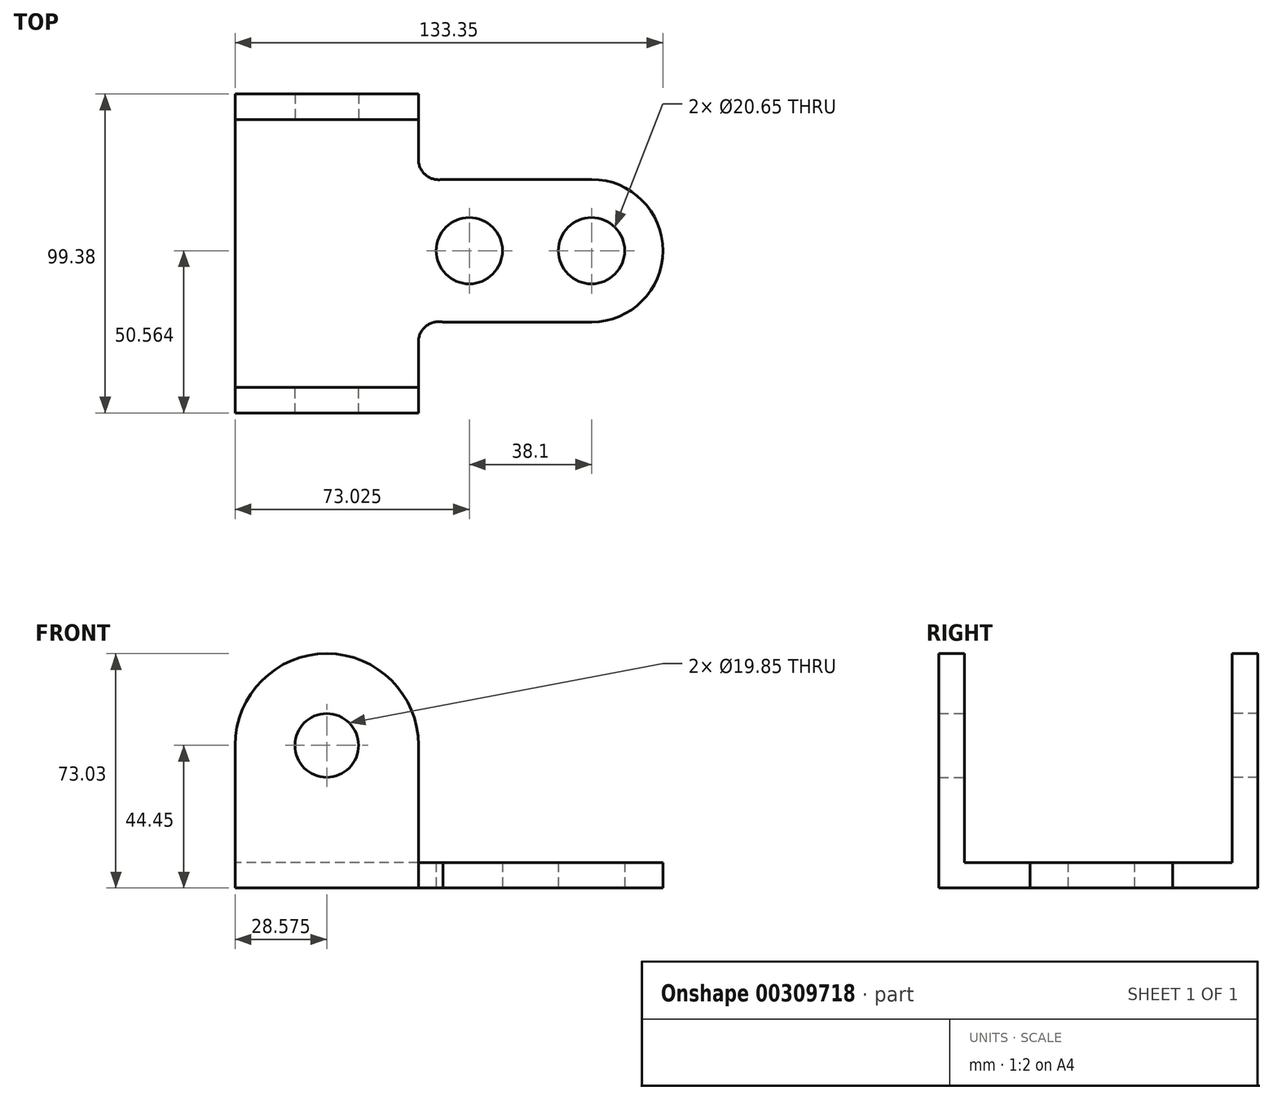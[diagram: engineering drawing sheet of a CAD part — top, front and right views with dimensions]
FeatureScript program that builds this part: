
annotation { "Feature Type Name" : "Feature", "Feature Type Description" : "" }
export const myFeature = defineFeature(function(context is Context, id is Id, definition is map)
    precondition{}
    {
        {
            var Q0;
            Q0=qCreatedBy(makeId("Top.planeOp"),FACE);
            var sketch = newSketch(context, id + "F0", { "sketchPlane" : qUnion([Q0])});
            skLineSegment(sketch, "E0", {"start": v(0, 0) * mm, "end": v(57.15, 0) * mm});
            skLineSegment(sketch, "E1", {"start": v(0, 18.14) * mm, "end": v(57.15, 18.14) * mm});
            skLineSegment(sketch, "E2", {"start": v(0, 0) * mm, "end": v(0, 91.44) * mm});
            skLineSegment(sketch, "E3", {"start": v(0, 91.44) * mm, "end": v(57.15, 91.44) * mm});
            skLineSegment(sketch, "E4", {"start": v(57.15, 91.44) * mm, "end": v(57.15, 75.04) * mm});
            skLineSegment(sketch, "E5", {"start": v(57.15, 75.04) * mm, "end": v(0, 75.04) * mm});
            skLineSegment(sketch, "E6", {"start": v(57.15, 18.14) * mm, "end": v(57.15, 0) * mm});
            skLineSegment(sketch, "E7", {"start": v(64.76, 68.82) * mm, "end": v(111.12, 68.82) * mm});
            skLineSegment(sketch, "E8", {"start": v(64.76, 24.37) * mm, "end": v(111.12, 24.37) * mm});
            skArc(sketch, "E9", {"start": v(111.12, 24.37) * mm, "mid": v(133.35, 46.6) * mm, "end": v(111.12, 68.82) * mm});
            skArc(sketch, "E10", {"start": v(57.15, 75.04) * mm, "mid": v(59.48, 70.13) * mm, "end": v(64.76, 68.82) * mm});
            skArc(sketch, "E11", {"start": v(64.76, 24.37) * mm, "mid": v(59.48, 23.06) * mm, "end": v(57.15, 18.14) * mm});
            skCircle(sketch, "E12", {"center": v(73.03, 46.6) * mm, "radius": 10.33 * mm});
            skCircle(sketch, "E13", {"center": v(111.12, 46.6) * mm, "radius": 10.33 * mm});
            skSolve(sketch);
        }
        {
            var Q0;
            Q0 = qSketchRegion(id + "F0", true);
            extrude(context, id + "F1", {"entities" : qUnion([Q0]), "depth" : 7.94 * mm});
        }
        {
            var Q0;
            Q0=makeQuery(id+"F1.opExtrude","SWEPT_FACE",FACE,{"disambiguationData":[OSD([sQuery(id+"F0.wireOp",EDGE,"E0")])]});
            var sketch = newSketch(context, id + "F2", { "sketchPlane" : qUnion([Q0])});
            skLineSegment(sketch, "E14", {"start": v(0, 0) * mm, "end": v(0, 44.45) * mm});
            skLineSegment(sketch, "E15", {"start": v(57.15, 0) * mm, "end": v(57.15, 44.45) * mm});
            skArc(sketch, "E16", {"start": v(57.15, 44.45) * mm, "mid": v(28.58, 73.03) * mm, "end": v(0, 44.45) * mm});
            skCircle(sketch, "E17", {"center": v(28.58, 44.45) * mm, "radius": 9.92 * mm});
            skSolve(sketch);
        }
        {
            var Q0;
            {var subQ1=sQuery(id+"F0.wireOp",EDGE,"E0");var subQ2=makeQuery(id+"F1.opExtrude","CAP_EDGE",EDGE,{"disambiguationData":[OSD([subQ1])],"isStart":true});Q0=makeQuery(id+"F2.imprint","IMPRINT",FACE,{"disambiguationData":[TD([[makeQuery(id+"F2.imprint","IMPRINT",EDGE,{"derivedFrom":subQ2}),1.0]])]});}
            var Q1;
            {var subQ0=sQuery(id+"F2.wireOp",EDGE,"E16");Q1=makeQuery(id+"F2.imprint","IMPRINT",FACE,{"disambiguationData":[TD([[makeQuery(id+"F2.imprint","IMPRINT",EDGE,{"derivedFrom":subQ0}),1.0]])]});}
            extrude(context, id + "F3", {"entities" : qUnion([Q0, Q1]), "operationType" : NewBodyOperationType.ADD, "endBound" : BoundingType.SYMMETRIC, "depth" : 7.94 * mm});
        }
        {
            var Q0;
            Q0=makeQuery(id+"F1.opExtrude","SWEPT_FACE",FACE,{"disambiguationData":[OSD([sQuery(id+"F0.wireOp",EDGE,"E3")])]});
            var sketch = newSketch(context, id + "F4", { "sketchPlane" : qUnion([Q0])});
            skLineSegment(sketch, "E18", {"start": v(-57.15, 0) * mm, "end": v(-57.15, 44.45) * mm});
            skPoint(sketch, "E18.endSnap0", {"position": v(-57.15, 3.97) * mm});
            skLineSegment(sketch, "E19", {"start": v(0, 0) * mm, "end": v(0, 44.45) * mm});
            skArc(sketch, "E20", {"start": v(0, 44.45) * mm, "mid": v(-28.58, 73.03) * mm, "end": v(-57.15, 44.45) * mm});
            skCircle(sketch, "E21", {"center": v(-28.58, 44.45) * mm, "radius": 9.92 * mm});
            skSolve(sketch);
        }
        {
            var Q0;
            {var subQ1=sQuery(id+"F0.wireOp",EDGE,"E3");var subQ2=makeQuery(id+"F1.opExtrude","CAP_EDGE",EDGE,{"disambiguationData":[OSD([subQ1])],"isStart":true});Q0=makeQuery(id+"F4.imprint","IMPRINT",FACE,{"disambiguationData":[TD([[makeQuery(id+"F4.imprint","IMPRINT",EDGE,{"derivedFrom":subQ2}),-1.0]])]});}
            var Q1;
            {var subQ0=sQuery(id+"F4.wireOp",EDGE,"E20");Q1=makeQuery(id+"F4.imprint","IMPRINT",FACE,{"disambiguationData":[TD([[makeQuery(id+"F4.imprint","IMPRINT",EDGE,{"derivedFrom":subQ0}),1.0]])]});}
            extrude(context, id + "F5", {"entities" : qUnion([Q0, Q1]), "operationType" : NewBodyOperationType.ADD, "endBound" : BoundingType.SYMMETRIC, "depth" : 7.94 * mm});
        }
    });
